# Revit family: РИДАН_NRV-R_Клапан обратный латунный пружинный муфтовый
name_source: partatom
category: Арматура трубопроводов
units: mm (PartAtom-declared; Revit-internal decimal feet)

## family parameters
Всегда вертикально = Да
На основе рабочей плоскости = Нет
Общий = Нет
При загрузке вырезать с полостями = Нет
Размер круглого соединителя = Использовать диаметр
Тип детали = Вставляется

## types (6) — shared parameters
ADSK_Версия Revit = 2019
ADSK_Версия семейства = 1.0
ADSK_Единица измерения = шт.
ADSK_Завод-изготовитель = ООО «Ридан-Трейд»
ADSK_Количество = 1
ADSK_Материал = Латунь корпус
ADSK_Потеря давления жидкости = 0.0 Па
ADSK_Расход жидкости = 0.0000 м³/ч
LT = NRV-R
URL = https://ridan.ru

## per-type parameters (varying)
| type | ADSK_Диаметр условный | ADSK_Код изделия | ADSK_Марка | ADSK_Масса | ADSK_Наименование | ADSK_Пропускная способность | a | b | c | d | e | f | g | УГО_Длина |
| DN15 | 15 мм | 065B8324R | NRV-R DN15 | 0.133 | Обратный клапан NRV-R пружинный с внутренней резьбой PN25, Tmax=110C, DN15 | 4.0000 м³/ч | 45 мм | 11 мм | 33 мм | 25 мм | 19 мм | 24 мм | 17 мм | 24 мм |
| DN20 | 20 мм | 065B8325R | NRV-R DN20 | 0.18 | Обратный клапан NRV-R пружинный с внутренней резьбой PN25, Tmax=110C, DN20 | 8.0000 м³/ч | 49 мм | 11 мм | 42 мм | 30 мм | 24 мм | 28 мм | 21 мм | 28 мм |
| DN25 | 25 мм | 065B8326R | NRV-R DN25 | 0.26 | Обратный клапан NRV-R пружинный с внутренней резьбой PN25, Tmax=110C, DN25 | 10.3000 м³/ч | 53 мм | 12 мм | 47 мм | 37 мм | 30 мм | 29 мм | 24 мм | 29 мм |
| DN32 | 32 мм | 065B8327R | NRV-R DN32 | 0.39 | Обратный клапан NRV-R пружинный с внутренней резьбой PN25, Tmax=110C, DN32 | 18.0000 м³/ч | 60 мм | 14 мм | 57 мм | 46 мм | 39 мм | 33 мм | 29 мм | 33 мм |
| DN40 | 40 мм | 065B8328R | NRV-R DN40 | 0.59 | Обратный клапан NRV-R пружинный с внутренней резьбой PN25, Tmax=110C, DN40 | 24.0000 м³/ч | 65 мм | 15 мм | 68 мм | 53 мм | 45 мм | 36 мм | 34 мм | 36 мм |
| DN50 | 50 мм | 065B8329R | NRV-R DN50 | 0.85 | Обратный клапан NRV-R пружинный с внутренней резьбой PN25, Tmax=110C, DN50 | 40.0000 м³/ч | 73 мм | 15 мм | 79 мм | 65 мм | 57 мм | 43 мм | 40 мм | 43 мм |
